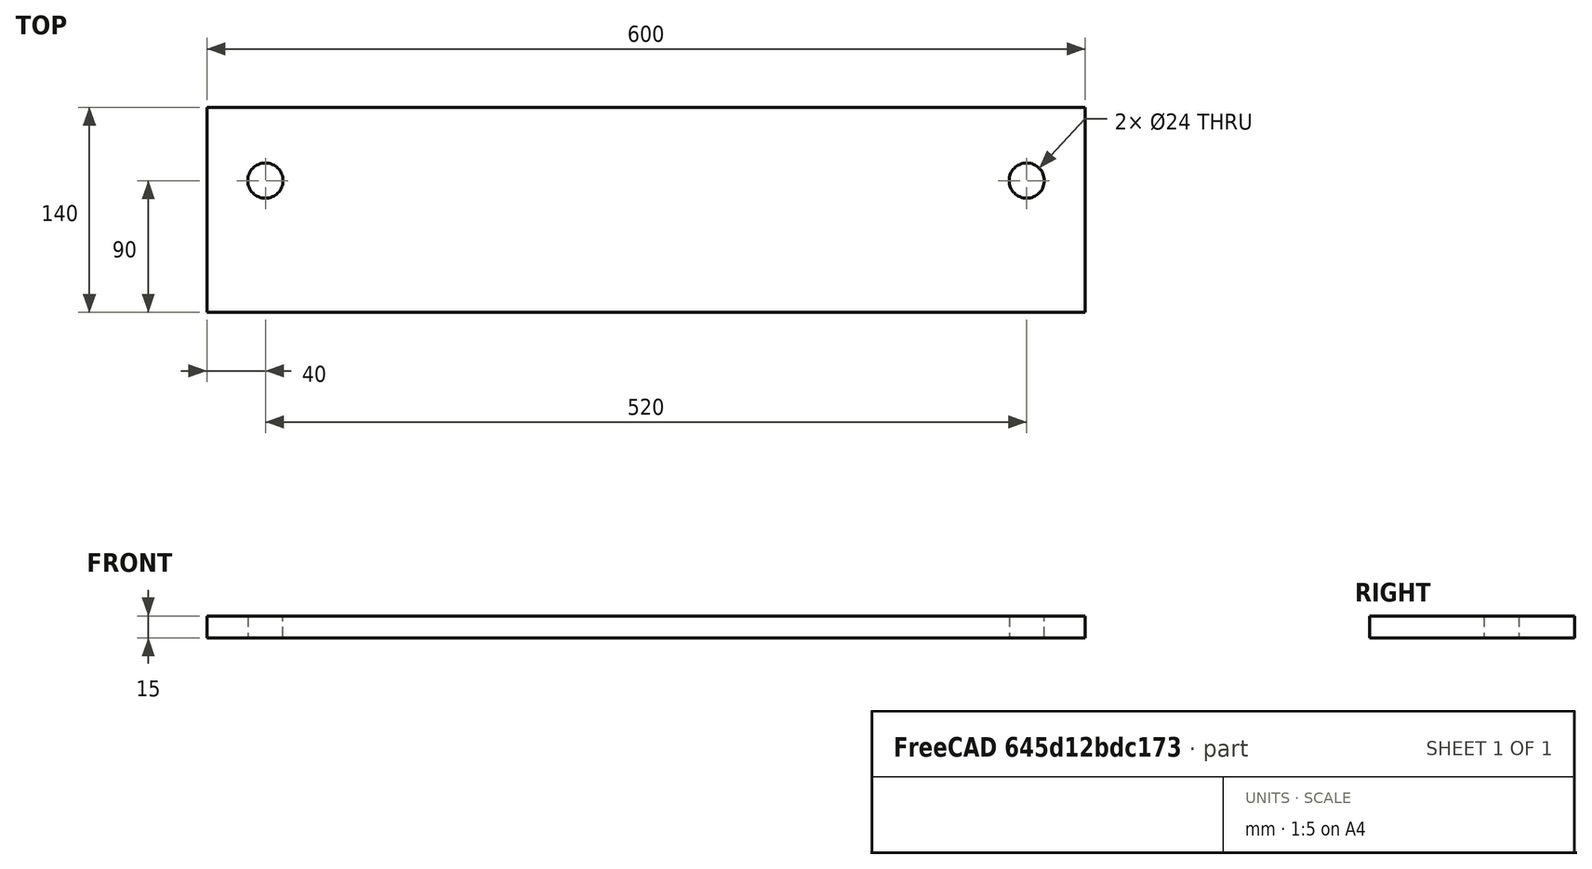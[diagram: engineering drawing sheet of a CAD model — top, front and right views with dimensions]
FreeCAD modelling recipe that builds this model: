
FCSTD DOCUMENT  (FreeCAD 1.0R39319 (Git))
Label: ctrl_panel_bottom
License: All rights reserved
LicenseURL: http://en.wikipedia.org/wiki/All_rights_reserved
objects: Sketcher::SketchObject×1, PartDesign::Pad×1, PartDesign::Body×1
note: 6 computed .brp shape members not serialized (recipe doc carries the construction recipe); baked Part::Feature solids carry a one-line shape summary decoded from their .brp

FEATURE [Sketcher::SketchObject] Sketch  label="ctrl_panel_bottom_sketch"
  ArcFitTolerance = 0
  AttachmentSupport = -> [XY_Plane]
  FullyConstrained = true
  MakeInternals = false
  MapMode = 5
  sketch-geometry (10):
    g0: LineSegment StartX=0 StartY=0 StartZ=0 EndX=600 EndY=0 EndZ=0
    g1: LineSegment StartX=600 StartY=0 StartZ=0 EndX=600 EndY=140 EndZ=0
    g2: LineSegment StartX=600 StartY=140 StartZ=0 EndX=0 EndY=140 EndZ=0
    g3: LineSegment StartX=0 StartY=140 StartZ=0 EndX=0 EndY=0 EndZ=0
    g4: Circle CenterX=40 CenterY=90 CenterZ=0 NormalX=0 NormalY=0 NormalZ=1 AngleXU=0 Radius=12
    g5: Circle CenterX=560 CenterY=90 CenterZ=0 NormalX=0 NormalY=0 NormalZ=1 AngleXU=0 Radius=12
    g6: LineSegment [constr] StartX=40 StartY=90 StartZ=0 EndX=0 EndY=90 EndZ=0
    g7: LineSegment [constr] StartX=40 StartY=90 StartZ=0 EndX=40 EndY=140 EndZ=0
    g8: LineSegment [constr] StartX=560 StartY=90 StartZ=0 EndX=560 EndY=140 EndZ=0
    g9: LineSegment [constr] StartX=560 StartY=90 StartZ=0 EndX=600 EndY=90 EndZ=0
  constraints (29):
    c: Coincident(g0,g1)
    c: Coincident(g1,g2)
    c: Coincident(g2,g3)
    c: Coincident(g3,g0)
    c: Horizontal(g0)
    c: Horizontal(g2)
    c: Vertical(g1)
    c: Vertical(g3)
    c: Coincident(g0,g-1)
    c: DistanceX(g0,g0) = 600
    c: DistanceY(g3,g3) = 140
    c: Radius(g4) = 12
    c: Radius(g5) = 12
    c: Coincident(g6,g4)
    c: PointOnObject(g6,g3)
    c: Horizontal(g6)
    c: PointOnObject(g7,g2)
    c: Vertical(g7)
    c: Coincident(g8,g5)
    c: PointOnObject(g8,g2)
    c: Vertical(g8)
    c: Coincident(g9,g5)
    c: PointOnObject(g9,g1)
    c: Horizontal(g9)
    c: Equal(g6,g9)
    c: Equal(g8,g7)
    c: DistanceY(g7,g7) = 50
    c: Coincident(g7,g4)
    c: DistanceX(g6,g6) = 40
FEATURE [PartDesign::Pad] Pad  label="ctrl_panel_pad"
  AllowMultiFace = false
  Direction = (0,0,1)
  Length = 15
  Length2 = 100
  Profile = -> Sketch
  ReferenceAxis = -> Sketch [N_Axis]
  Suppressed = false
  Type = 0
FEATURE [PartDesign::Body] Body  label="ctrl_panel_body"
  AllowCompound = false
  Group = -> [Sketch,Pad]
  Origin = -> Origin
  Tip = -> Pad
